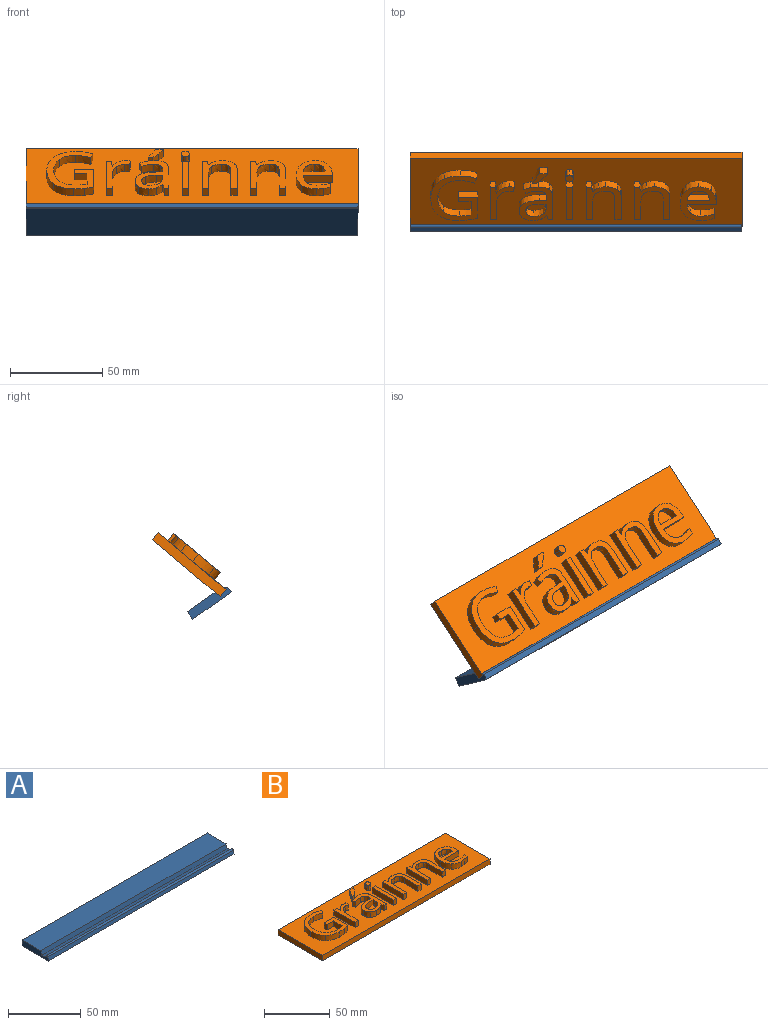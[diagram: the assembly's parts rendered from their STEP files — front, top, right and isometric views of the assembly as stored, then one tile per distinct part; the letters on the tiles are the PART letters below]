
ASSEMBLY  parts=2 mates=1
PART A: 11 faces, bbox 180x26x5 mm
  f0: plane 180x25mm, normal (0,0,-1), area 4500mm2, adj f1,f5,f6,f8
  f1: plane 180x5mm, normal (0,1,0), area 900mm2, adj f0,f2,f5,f6
  f2: plane 180x18.28mm, normal (0,0,1), area 3289.8mm2, adj f1,f3,f5,f6
  f3: plane 180x3.5mm, normal (0,-0.97,0.26), area 652.2mm2, adj f2,f4,f5,f6
  f4: plane 180x5.02mm, normal (0,0.26,0.97), area 936mm2, adj f3,f5,f6,f7
  f5: plane 25.97x5mm, normal (1,0,0), area 110.2mm2, adj f0,f1,f2,f3,f4,f7,f8,f9
  f6: plane 25.97x5mm, normal (-1,0,0), area 110.2mm2, adj f0,f1,f2,f3,f4,f7,f8,f9
  f7: plane 180x1.02mm, normal (0,0.97,-0.26), area 189.7mm2, adj f4,f5,f6,f10
  f8: plane 180x0.97mm, normal (0,-0.26,-0.97), area 180mm2, adj f0,f5,f6,f9
  f9: plane 180x2.9mm, normal (0,-0.97,0.26), area 540mm2, adj f5,f6,f8,f10
  f10: cylinder r=1mm len=180mm, axis (1,0,0), area 282.7mm2, adj f5,f6,f7,f9
PART B: 150 faces, bbox 180x48x10 mm
  f0: plane 180x48mm, normal (0,0,1), area 7193.3mm2, adj f1,f2,f3,f4,f6,f7,f8,f9
  f1: plane 48x5mm, normal (1,0,0), area 240mm2, adj f0,f2,f4,f5
  f2: plane 180x5mm, normal (0,1,0), area 900mm2, adj f0,f1,f3,f5
  f3: plane 48x5mm, normal (-1,0,0), area 240mm2, adj f0,f2,f4,f5
  f4: plane 180x5mm, normal (0,-1,0), area 900mm2, adj f0,f1,f3,f5
  f5: plane 180x48mm, normal (0,0,-1), area 8640mm2, adj f1,f2,f3,f4
  f6: plane 10.36x5mm, normal (0,1,0), area 51.8mm2, adj f0,f7,f25,f26
  f7: plane 5x3.17mm, normal (-1,0,0), area 15.8mm2, adj f0,f6,f8,f26
  f8: plane 6.81x5mm, normal (0,-1,0), area 34.1mm2, adj f0,f7,f9,f26
  f9: plane 9.38x5mm, normal (-1,0,0), area 46.9mm2, adj f0,f8,f10,f26
  f10: extruded ~6.19x5mm, area 31.3mm2, adj f0,f9,f11,f26
  f11: extruded ~8.85x5mm, area 48.4mm2, adj f0,f10,f12,f26
  f12: extruded ~9.36x5mm, area 50.4mm2, adj f0,f11,f13,f26
  f13: extruded ~9.2x5mm, area 49.8mm2, adj f0,f12,f14,f26
  f14: extruded ~8.7x5mm, area 47.9mm2, adj f0,f13,f15,f26
  f15: extruded ~7.95x5mm, area 41mm2, adj f0,f14,f16,f26
  f16: plane 5x3.13mm, normal (0.92,-0.4,0), area 17.1mm2, adj f0,f15,f17,f26
  f17: extruded ~9.1x5mm, area 46.7mm2, adj f0,f16,f18,f26
  f18: extruded ~8.4x5mm, area 43.5mm2, adj f0,f17,f19,f26
  f19: extruded ~5.5x5.46mm, area 39.3mm2, adj f0,f18,f20,f26
  f20: extruded ~8.33x5mm, area 43.2mm2, adj f0,f19,f21,f26
  f21: extruded ~11.54x5mm, area 62.3mm2, adj f0,f20,f22,f26
  f22: extruded ~10.78x5mm, area 59.4mm2, adj f0,f21,f23,f26
  f23: extruded ~5.8x5mm, area 29.1mm2, adj f0,f22,f24,f26
  f24: extruded ~5x4.92mm, area 25.3mm2, adj f0,f23,f25,f26
  f25: plane 14.83x5mm, normal (1,0,0), area 74.1mm2, adj f0,f6,f24,f26
  f26: plane 31.34x25.36mm, normal (0,0,1), area 281.4mm2, adj f6,f7,f8,f9,f10,f11,f12,f13
  f27: extruded ~5x2.73mm, area 13.7mm2, adj f0,f28,f39,f40
  f28: extruded ~5x3.94mm, area 20.9mm2, adj f0,f27,f29,f40
  f29: extruded ~5x3.44mm, area 23.2mm2, adj f0,f28,f30,f40
  f30: plane 5x0.17mm, normal (0,1,0), area 0.8mm2, adj f0,f29,f31,f40
  f31: plane 5x4.23mm, normal (1,0.09,0), area 21.2mm2, adj f0,f30,f32,f40
  f32: plane 5x2.86mm, normal (0,1,0), area 14.3mm2, adj f0,f31,f33,f40
  f33: plane 22.86x5mm, normal (-1,0,0), area 114.3mm2, adj f0,f32,f34,f40
  f34: plane 5x3.46mm, normal (0,-1,0), area 17.3mm2, adj f0,f33,f35,f40
  f35: plane 12.27x5mm, normal (1,0,0), area 61.3mm2, adj f0,f34,f36,f40
  f36: extruded ~5.61x5mm, area 30.4mm2, adj f0,f35,f37,f40
  f37: extruded ~5x4.74mm, area 27.1mm2, adj f0,f36,f38,f40
  f38: extruded ~5x2.5mm, area 12.6mm2, adj f0,f37,f39,f40
  f39: plane 5x3.21mm, normal (0.99,-0.15,0), area 16.2mm2, adj f0,f27,f38,f40
  f40: plane 23.28x13.16mm, normal (0,0,1), area 108.9mm2, adj f27,f28,f29,f30,f31,f32,f33,f34
  f41: extruded ~5.08x5mm, area 27.6mm2, adj f42,f67,f68,f69
  f42: extruded ~5x3.18mm, area 17mm2, adj f41,f43,f68,f69
  f43: extruded ~5x2.86mm, area 15.9mm2, adj f42,f44,f68,f69
  f44: extruded ~5x3.53mm, area 20.8mm2, adj f43,f45,f68,f69
  f45: extruded ~5.95x5mm, area 30.8mm2, adj f44,f46,f68,f69
  f46: plane 5x3.46mm, normal (0.04,-1,0), area 17.3mm2, adj f45,f47,f68,f69
  f47: plane 5x2.06mm, normal (-1,0,0), area 10.3mm2, adj f46,f67,f68,f69
  f48: plane 5x3.26mm, normal (-0.98,-0.21,0), area 16.6mm2, adj f0,f49,f66,f68
  f49: plane 5x2.57mm, normal (0,-1,0), area 12.8mm2, adj f0,f48,f50,f68
  f50: plane 15.6x5mm, normal (1,0,0), area 78mm2, adj f0,f49,f51,f68
  f51: extruded ~5.82x5mm, area 31.6mm2, adj f0,f50,f52,f68
  f52: extruded ~6.06x5mm, area 32.3mm2, adj f0,f51,f53,f68
  f53: extruded ~5x4.04mm, area 20.4mm2, adj f0,f52,f54,f68
  f54: extruded ~5x3.7mm, area 19.9mm2, adj f0,f53,f55,f68
  f55: plane 5x2.65mm, normal (-0.93,-0.37,0), area 14.3mm2, adj f0,f54,f56,f68
  f56: extruded ~6.46x5mm, area 33.7mm2, adj f0,f55,f57,f68
  f57: extruded ~5x3.7mm, area 20.2mm2, adj f0,f56,f58,f68
  f58: extruded ~5x3.97mm, area 21.1mm2, adj f0,f57,f59,f68
  f59: plane 5x1.42mm, normal (-1,0,0), area 7.1mm2, adj f0,f58,f60,f68
  f60: plane 5x3.88mm, normal (-0.03,1,0), area 19.4mm2, adj f0,f59,f61,f68
  f61: extruded ~11.07x7.25mm, area 74.4mm2, adj f0,f60,f62,f68
  f62: extruded ~5x4.98mm, area 27.6mm2, adj f0,f61,f63,f68
  f63: extruded ~5.33x5mm, area 28.7mm2, adj f0,f62,f64,f68
  f64: extruded ~5x4.25mm, area 21.7mm2, adj f0,f63,f65,f68
  f65: extruded ~5x3.41mm, area 22.6mm2, adj f0,f64,f66,f68
  f66: plane 5x0.17mm, normal (0,-1,0), area 0.8mm2, adj f0,f48,f65,f68
  f67: extruded ~5x4.96mm, area 27.2mm2, adj f41,f47,f68,f69
  f68: plane 23.65x18.33mm, normal (0,0,1), area 204.7mm2, adj f41,f42,f43,f44,f45,f46,f47,f48
  f69: plane 11.24x8.8mm, normal (0,0,1), area 79.7mm2, adj f41,f42,f43,f44,f45,f46,f47,f67
  f70: extruded ~5x3.13mm, area 19mm2, adj f0,f71,f77,f78
  f71: plane 5x0.52mm, normal (-1,0,0), area 2.6mm2, adj f0,f70,f72,f78
  f72: plane 5x2.32mm, normal (0,-1,0), area 11.6mm2, adj f0,f71,f73,f78
  f73: extruded ~5x3.15mm, area 22mm2, adj f0,f72,f74,f78
  f74: extruded ~5x3.34mm, area 21.6mm2, adj f0,f73,f75,f78
  f75: plane 5x0.43mm, normal (1,0,0), area 2.2mm2, adj f0,f74,f76,f78
  f76: plane 5x4.21mm, normal (0,1,0), area 21.1mm2, adj f0,f75,f77,f78
  f77: extruded ~5x3.19mm, area 18.4mm2, adj f0,f70,f76,f78
  f78: plane 8.19x6.84mm, normal (0,0,1), area 25.3mm2, adj f70,f71,f72,f73,f74,f75,f76,f77
  f79: plane 5x3.46mm, normal (0,-1,0), area 17.3mm2, adj f0,f80,f82,f83
  f80: plane 22.86x5mm, normal (1,0,0), area 114.3mm2, adj f0,f79,f81,f83
  f81: plane 5x3.46mm, normal (0,1,0), area 17.3mm2, adj f0,f80,f82,f83
  f82: plane 22.86x5mm, normal (-1,0,0), area 114.3mm2, adj f0,f79,f81,f83
  f83: plane 22.86x3.46mm, normal (0,0,1), area 79.2mm2, adj f79,f80,f81,f82
  f84: extruded ~5x1.74mm, area 9.4mm2, adj f0,f85,f91,f92
  f85: extruded ~5x1.74mm, area 9.4mm2, adj f0,f84,f86,f92
  f86: extruded ~5x1.46mm, area 8.1mm2, adj f0,f85,f87,f92
  f87: extruded ~5x1.44mm, area 7.9mm2, adj f0,f86,f88,f92
  f88: extruded ~5x1.74mm, area 9.5mm2, adj f0,f87,f89,f92
  f89: extruded ~5x1.73mm, area 9.4mm2, adj f0,f88,f90,f92
  f90: extruded ~5x1.44mm, area 7.9mm2, adj f0,f89,f91,f92
  f91: extruded ~5x1.46mm, area 8mm2, adj f0,f84,f90,f92
  f92: plane 4.61x4.09mm, normal (0,0,1), area 15.4mm2, adj f84,f85,f86,f87,f88,f89,f90,f91
  f93: plane 14.79x5mm, normal (-1,0,0), area 73.9mm2, adj f0,f94,f109,f110
  f94: plane 5x3.46mm, normal (0,-1,0), area 17.3mm2, adj f0,f93,f95,f110
  f95: plane 14.91x5mm, normal (1,0,0), area 74.5mm2, adj f0,f94,f96,f110
  f96: extruded ~6.38x5mm, area 34.5mm2, adj f0,f95,f97,f110
  f97: extruded ~6.22x5mm, area 33.4mm2, adj f0,f96,f98,f110
  f98: extruded ~5x4.27mm, area 22.1mm2, adj f0,f97,f99,f110
  f99: extruded ~5x2.99mm, area 20.1mm2, adj f0,f98,f100,f110
  f100: plane 5x0.17mm, normal (0,1,0), area 0.8mm2, adj f0,f99,f101,f110
  f101: plane 5x3.13mm, normal (0.98,0.18,0), area 15.9mm2, adj f0,f100,f102,f110
  f102: plane 5x2.82mm, normal (0,1,0), area 14.1mm2, adj f0,f101,f103,f110
  f103: plane 22.86x5mm, normal (-1,0,0), area 114.3mm2, adj f0,f102,f104,f110
  f104: plane 5x3.46mm, normal (0,-1,0), area 17.3mm2, adj f0,f103,f105,f110
  f105: plane 11.99x5mm, normal (1,0,0), area 60mm2, adj f0,f104,f106,f110
  f106: extruded ~6.4x5mm, area 33.7mm2, adj f0,f105,f107,f110
  f107: extruded ~5.25x5mm, area 28.9mm2, adj f0,f106,f108,f110
  f108: extruded ~5x3.99mm, area 21.7mm2, adj f0,f107,f109,f110
  f109: extruded ~5x4.17mm, area 22.3mm2, adj f0,f93,f108,f110
  f110: plane 23.28x19.11mm, normal (0,0,1), area 189.4mm2, adj f93,f94,f95,f96,f97,f98,f99,f100
  f111: plane 14.79x5mm, normal (-1,0,0), area 73.9mm2, adj f0,f112,f127,f128
  f112: plane 5x3.46mm, normal (0,-1,0), area 17.3mm2, adj f0,f111,f113,f128
  f113: plane 14.91x5mm, normal (1,0,0), area 74.5mm2, adj f0,f112,f114,f128
  f114: extruded ~6.38x5mm, area 34.5mm2, adj f0,f113,f115,f128
  f115: extruded ~6.22x5mm, area 33.4mm2, adj f0,f114,f116,f128
  f116: extruded ~5x4.27mm, area 22.1mm2, adj f0,f115,f117,f128
  f117: extruded ~5x2.99mm, area 20.1mm2, adj f0,f116,f118,f128
  f118: plane 5x0.17mm, normal (0,1,0), area 0.8mm2, adj f0,f117,f119,f128
  f119: plane 5x3.13mm, normal (0.98,0.18,0), area 15.9mm2, adj f0,f118,f120,f128
  f120: plane 5x2.82mm, normal (0,1,0), area 14.1mm2, adj f0,f119,f121,f128
  f121: plane 22.86x5mm, normal (-1,0,0), area 114.3mm2, adj f0,f120,f122,f128
  f122: plane 5x3.46mm, normal (0,-1,0), area 17.3mm2, adj f0,f121,f123,f128
  f123: plane 11.99x5mm, normal (1,0,0), area 60mm2, adj f0,f122,f124,f128
  f124: extruded ~6.4x5mm, area 33.7mm2, adj f0,f123,f125,f128
  f125: extruded ~5.25x5mm, area 28.9mm2, adj f0,f124,f126,f128
  f126: extruded ~5x3.99mm, area 21.7mm2, adj f0,f125,f127,f128
  f127: extruded ~5x4.17mm, area 22.3mm2, adj f0,f111,f126,f128
  f128: plane 23.28x19.11mm, normal (0,0,1), area 189.4mm2, adj f111,f112,f113,f114,f115,f116,f117,f118
  f129: extruded ~5x4.39mm, area 24.4mm2, adj f130,f147,f148,f149
  f130: extruded ~5x4.17mm, area 23.4mm2, adj f129,f131,f148,f149
  f131: extruded ~5.01x5mm, area 26.6mm2, adj f130,f132,f148,f149
  f132: plane 11.95x5mm, normal (0,1,0), area 59.8mm2, adj f131,f147,f148,f149
  f133: extruded ~8x5mm, area 44.1mm2, adj f0,f134,f146,f148
  f134: extruded ~5x3.95mm, area 19.9mm2, adj f0,f133,f135,f148
  f135: extruded ~5x3.47mm, area 18.3mm2, adj f0,f134,f136,f148
  f136: plane 5x3.09mm, normal (1,0,0), area 15.4mm2, adj f0,f135,f137,f148
  f137: extruded ~7.29x5mm, area 37.5mm2, adj f0,f136,f138,f148
  f138: extruded ~5.43x5mm, area 30mm2, adj f0,f137,f139,f148
  f139: extruded ~6.11x5mm, area 32.9mm2, adj f0,f138,f140,f148
  f140: plane 15.74x5mm, normal (0,-1,0), area 78.7mm2, adj f0,f139,f141,f148
  f141: plane 5x2.19mm, normal (1,0,0), area 10.9mm2, adj f0,f140,f142,f148
  f142: extruded ~7.46x5mm, area 40.2mm2, adj f0,f141,f143,f148
  f143: extruded ~6.79x5mm, area 38mm2, adj f0,f142,f144,f148
  f144: extruded ~7.31x5mm, area 41.4mm2, adj f0,f143,f145,f148
  f145: extruded ~8.79x5mm, area 47mm2, adj f0,f144,f146,f148
  f146: extruded ~8.57x5mm, area 46.4mm2, adj f0,f133,f145,f148
  f147: extruded ~5x4.96mm, area 27.1mm2, adj f129,f132,f148,f149
  f148: plane 23.7x19.33mm, normal (0,0,1), area 208.4mm2, adj f129,f130,f131,f132,f133,f134,f135,f136
  f149: plane 11.95x6.75mm, normal (0,0,1), area 65.1mm2, adj f129,f130,f131,f132,f147
PLACE A rot(axis=(-1,0,0),35deg) t=(-96.28,-31.58,-4.17)mm
PLACE B rot(axis=(1,0,0),40deg) t=(-7.79,-17.83,16.34)mm
MATE fastened B.f5 <-> A.f3  axis (0,-0.64,0.77) through (-96.28,-36.22,0.91)mm
